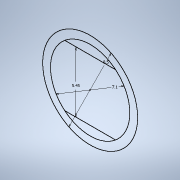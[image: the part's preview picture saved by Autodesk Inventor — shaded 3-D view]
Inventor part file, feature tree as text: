
AUTODESK INVENTOR PART (.ipt)
format: ipt  version: 2022 (Build 260153070, 153G)  size: 137,216 bytes
history: native  units: mm
features: extrude x2, sketch x2, fillet x1
ambient origin geometry x8: Origin, YZ Plane, XZ Plane, XY Plane, X Axis, Y Axis, Z Axis, Center Point
bodies: Solid1 (feature_tree)
feature tree (5):
  extrude  "Extrusion1"  Depth=5.45mm
  extrude  "Extrusion2"  Depth=1.25mm TaperAngle=0.0deg
  fillet  "Fillet1"  Radius=2.0mm
  sketch  "Sketch1"  dims[d0=7.1mm d1=5.45mm]
  sketch  "Sketch4"  dims[d2=8.5mm d3=1.25mm d4=0.0mm d7=2.0mm d8=1.25mm d9=0.0mm d10=1.0mm]
